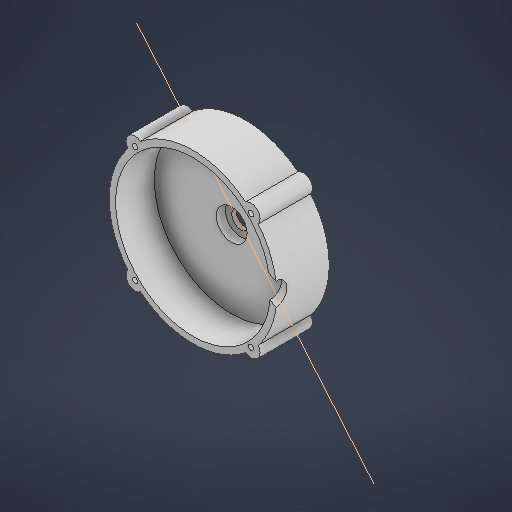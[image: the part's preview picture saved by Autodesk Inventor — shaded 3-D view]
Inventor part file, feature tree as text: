
AUTODESK INVENTOR PART (.ipt)
format: ipt  version: 2025.3 (Build 293356030, 356C)  size: 286,720 bytes
history: native  units: mm
features: sketch x5, extrude x4, plane x2, other x1
ambient origin geometry x8: Origin, YZ Plane, XZ Plane, XY Plane, X Axis, Y Axis, Z Axis, Center Point
bodies: Solid1 (feature_tree)
feature tree (12):
  sketch  "Sketch1"  dims[d1=40.0mm]
  extrude  "Extrusion1"  Depth=10.0mm TaperAngle=0.0deg
  extrude  "Extrusion2"  Depth=28.75mm TaperAngle=0.0deg
  extrude  "Extrusion3"  [1 undecoded]
  sketch  "Sketch2"  dims[d12=7.5mm d13=0.0mm d14=28.75mm d15=0.0mm]
  plane  "Work Plane1"
  sketch  "Sketch3"  dims[d16=-13.089969mm d17=-5.235988mm]
  plane  "Work Plane2"
  extrude  "Extrusion4"  Depth=30.0mm TaperAngle=0.0deg
  other  "Work Axis1"
  sketch  "Sketch Circular Pattern1"  dims[d2=10.0mm d3=16.9mm d4=85.0mm d5=90.0mm d6=2.9mm d7=5.0mm d8=360.0deg d9=92.0mm d10=2.5mm d11=0.0mm]
  sketch  "Sketch4"  dims[d18=10.65mm d19=30.0mm d20=0.0mm]
note: 1 required parameter value undecoded (feature->parameter linkage not recoverable at this tier; creation-order binding heuristic only, values carry confidence <= 0.55)
